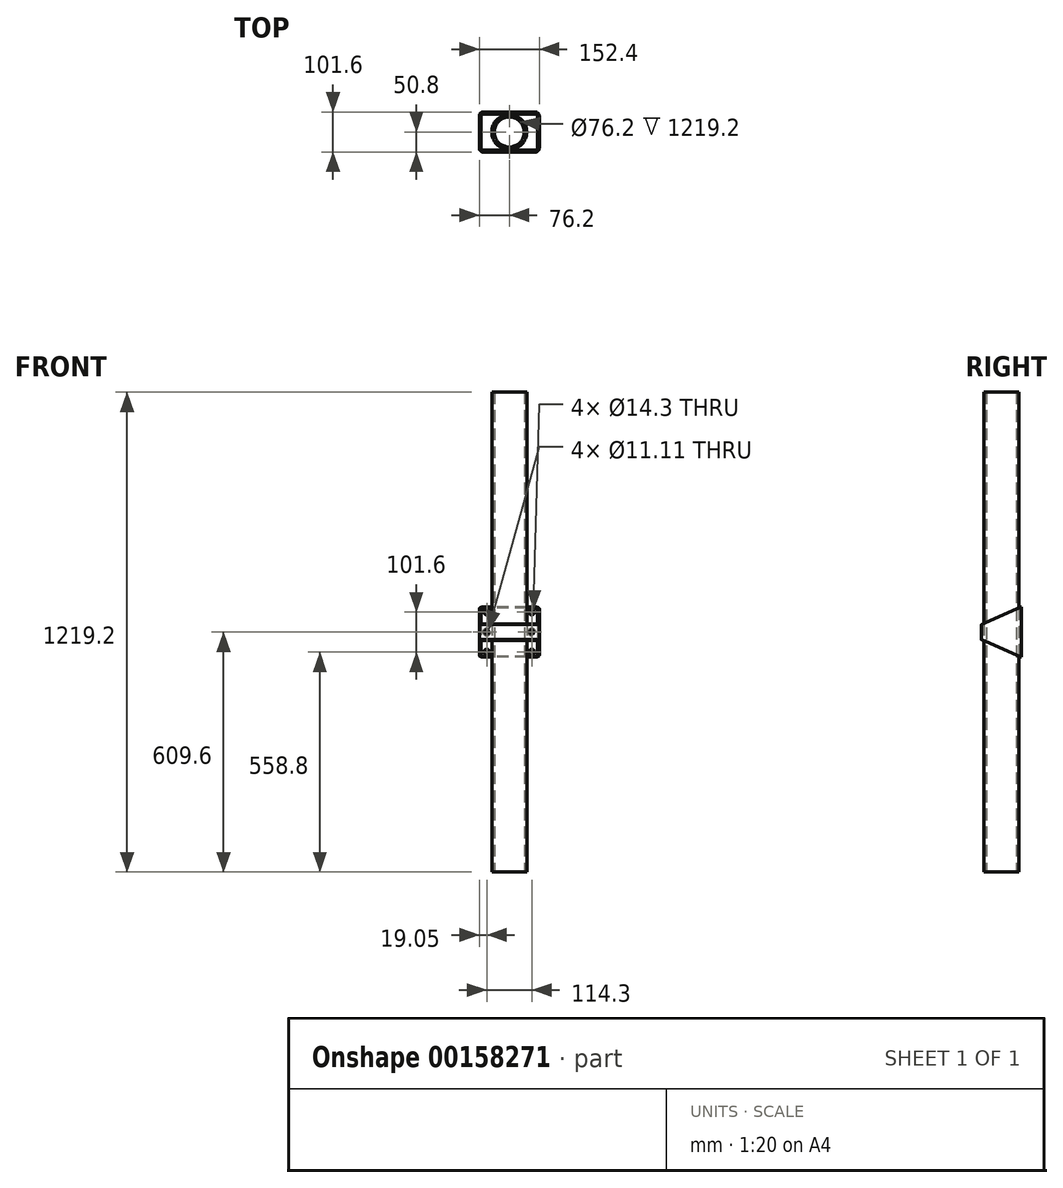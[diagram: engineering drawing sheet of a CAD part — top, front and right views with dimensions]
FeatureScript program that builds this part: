
annotation { "Feature Type Name" : "Feature", "Feature Type Description" : "" }
export const myFeature = defineFeature(function(context is Context, id is Id, definition is map)
    precondition{}
    {
        {
            var Q0;
            Q0=qCreatedBy(makeId("Top.planeOp"),FACE);
            var sketch = newSketch(context, id + "F0", { "sketchPlane" : qUnion([Q0])});
            skLineSegment(sketch, "E0.bottom", {"start": v(66.68, 50.8) * mm, "end": v(-66.67, 50.8) * mm});
            skLineSegment(sketch, "E0.top", {"start": v(66.67, -50.8) * mm, "end": v(-66.68, -50.8) * mm});
            skLineSegment(sketch, "E0.left", {"start": v(76.2, 41.28) * mm, "end": v(76.2, -41.28) * mm});
            skLineSegment(sketch, "E0.right", {"start": v(-76.2, 41.28) * mm, "end": v(-76.2, -41.27) * mm});
            skPoint(sketch, "E0.middle", {"position": v(0, 0) * mm});
            skPoint(sketch, "E1.visualSharp", {"position": v(-76.2, 50.8) * mm});
            skArc(sketch, "E1.filletArc", {"start": v(-66.67, 50.8) * mm, "mid": v(-73.41, 48.01) * mm, "end": v(-76.2, 41.28) * mm});
            skPoint(sketch, "E2.visualSharp", {"position": v(76.2, 50.8) * mm});
            skArc(sketch, "E2.filletArc", {"start": v(76.2, 41.28) * mm, "mid": v(73.41, 48.01) * mm, "end": v(66.68, 50.8) * mm});
            skPoint(sketch, "E3.visualSharp", {"position": v(76.2, -50.8) * mm});
            skArc(sketch, "E3.filletArc", {"start": v(66.67, -50.8) * mm, "mid": v(73.41, -48.01) * mm, "end": v(76.2, -41.28) * mm});
            skPoint(sketch, "E4.visualSharp", {"position": v(-76.2, -50.8) * mm});
            skArc(sketch, "E4.filletArc", {"start": v(-76.2, -41.27) * mm, "mid": v(-73.41, -48.01) * mm, "end": v(-66.68, -50.8) * mm});
            skArc(sketch, "E5.0", {"start": v(71.44, 41.27) * mm, "mid": v(70.04, 44.64) * mm, "end": v(66.68, 46.04) * mm});
            skLineSegment(sketch, "E5.1", {"start": v(66.68, 46.04) * mm, "end": v(-66.67, 46.04) * mm});
            skLineSegment(sketch, "E5.2", {"start": v(71.44, 41.27) * mm, "end": v(71.44, -41.28) * mm});
            skArc(sketch, "E5.3", {"start": v(-66.67, 46.04) * mm, "mid": v(-70.04, 44.64) * mm, "end": v(-71.44, 41.27) * mm});
            skArc(sketch, "E5.4", {"start": v(66.67, -46.04) * mm, "mid": v(70.04, -44.64) * mm, "end": v(71.44, -41.28) * mm});
            skLineSegment(sketch, "E5.5", {"start": v(66.67, -46.04) * mm, "end": v(-66.68, -46.04) * mm});
            skArc(sketch, "E5.6", {"start": v(-71.44, -41.28) * mm, "mid": v(-70.04, -44.64) * mm, "end": v(-66.68, -46.04) * mm});
            skLineSegment(sketch, "E5.7", {"start": v(-71.44, 41.27) * mm, "end": v(-71.44, -41.28) * mm});
            skSolve(sketch);
        }
        {
            var Q0;
            Q0=qCreatedBy(makeId("Right.planeOp"),FACE);
            var sketch = newSketch(context, id + "F1", { "sketchPlane" : qUnion([Q0])});
            skLineSegment(sketch, "E6", {"start": v(-50.52, 0) * mm, "end": v(-50.52, 19.05) * mm});
            skLineSegment(sketch, "E7", {"start": v(50.64, 0) * mm, "end": v(50.64, 63.5) * mm});
            skSolve(sketch);
        }
        {
            var Q0;
            Q0=qCreatedBy(makeId("Right.planeOp"),FACE);
            cPlane(context, id + "F2", {"entities" : qUnion([Q0]), "cplaneType" : CPlaneType.OFFSET, "offset" : 25.4 * mm, "width" : 152.4 * mm, "height" : 152.4 * mm});
        }
        {
            var Q0;
            Q0=qCreatedBy(id+"F2.planeOp",FACE);
            var sketch = newSketch(context, id + "F3", { "sketchPlane" : qUnion([Q0])});
            skLineSegment(sketch, "E8.0", {"start": v(50.64, 0) * mm, "end": v(50.64, 63.5) * mm});
            skSolve(sketch);
        }
        {
            var Q0;
            Q0=sQuery(id+"F1.wireOp",VERTEX,"E7.end");
            var Q1;
            Q1=sQuery(id+"F3.wireOp",VERTEX,"E8.0.end");
            var Q2;
            Q2=sQuery(id+"F1.wireOp",VERTEX,"E6.end");
            cPlane(context, id + "F4", {"entities" : qUnion([Q0, Q1, Q2]), "cplaneType" : CPlaneType.THREE_POINT, "offset" : 25.4 * mm, "width" : 152.4 * mm, "height" : 152.4 * mm});
        }
        {
            var Q0;
            Q0=makeQuery(id+"F0.imprint","IMPRINT",FACE,{"disambiguationData":[TD([[makeQuery(id+"F0.imprint","IMPRINT",EDGE,{"derivedFrom":sQuery(id+"F0.wireOp",EDGE,"E0.bottom")}),1.0]])]});
            var Q1;
            Q1=qCreatedBy(id+"F4.planeOp",FACE);
            extrude(context, id + "F5", {"entities" : qUnion([Q0]), "endBound" : BoundingType.UP_TO_SURFACE, "endBoundEntityFace" : qUnion([Q1]), "depth" : 25.4 * mm});
        }
        {
            var Q0;
            Q0=makeQuery(id+"F5.opExtrude","SWEPT_BODY",BODY,{"disambiguationData":[OSD([sQuery(id+"F0.wireOp",EDGE,"E0.bottom"),sQuery(id+"F0.wireOp",EDGE,"E0.top"),sQuery(id+"F0.wireOp",EDGE,"E0.left"),sQuery(id+"F0.wireOp",EDGE,"E0.right"),sQuery(id+"F0.wireOp",EDGE,"E1.filletArc"),sQuery(id+"F0.wireOp",EDGE,"E2.filletArc"),sQuery(id+"F0.wireOp",EDGE,"E3.filletArc"),sQuery(id+"F0.wireOp",EDGE,"E4.filletArc"),sQuery(id+"F0.wireOp",EDGE,"E5.0"),sQuery(id+"F0.wireOp",EDGE,"E5.1"),sQuery(id+"F0.wireOp",EDGE,"E5.2"),sQuery(id+"F0.wireOp",EDGE,"E5.3"),sQuery(id+"F0.wireOp",EDGE,"E5.4"),sQuery(id+"F0.wireOp",EDGE,"E5.5"),sQuery(id+"F0.wireOp",EDGE,"E5.6"),sQuery(id+"F0.wireOp",EDGE,"E5.7")])]});
            var Q1;
            Q1=qCreatedBy(makeId("Top.planeOp"),FACE);
            mirror(context, id + "F6", {"operationType" : NewBodyOperationType.ADD, "entities" : qUnion([Q0]), "mirrorPlane" : qUnion([Q1])});
        }
        {
            var Q0;
            Q0=qCreatedBy(makeId("Top.planeOp"),FACE);
            var sketch = newSketch(context, id + "F7", { "sketchPlane" : qUnion([Q0])});
            skCircle(sketch, "E9", {"center": v(0, 0) * mm, "radius": 44.45 * mm});
            skCircle(sketch, "E10.0", {"center": v(0, 0) * mm, "radius": 38.1 * mm});
            skSolve(sketch);
        }
        {
            var Q0;
            Q0 = qSketchRegion(id + "F7", true);
            extrude(context, id + "F8", {"entities" : qUnion([Q0]), "depth" : 609.6 * mm, "hasSecondDirection" : true, "secondDirectionOppositeDirection" : true, "secondDirectionDepth" : 609.6 * mm});
        }
        {
            var Q0;
            {var subQ0=makeQuery(id+"F5.opExtrude","SWEPT_FACE",FACE,{"disambiguationData":[OSD([sQuery(id+"F0.wireOp",EDGE,"E0.bottom")])]});Q0=makeQuery(id+"F6.boolean.opBoolean","MERGE",FACE,{"derivedFrom":[subQ0,makeQuery(id+"F6.opPattern","COPY",FACE,{"derivedFrom":subQ0,"instanceName":"1"})]});}
            var sketch = newSketch(context, id + "F9", { "sketchPlane" : qUnion([Q0])});
            skPoint(sketch, "E11", {"position": v(57.15, 0) * mm});
            skPoint(sketch, "E12", {"position": v(57.15, 50.8) * mm});
            skPoint(sketch, "E13.MirrorP", {"position": v(57.15, -50.8) * mm});
            skPoint(sketch, "E14.MirrorP", {"position": v(-57.15, 50.8) * mm});
            skPoint(sketch, "E15.MirrorP", {"position": v(-57.15, 0) * mm});
            skPoint(sketch, "E16.MirrorP", {"position": v(-57.15, -50.8) * mm});
            skSolve(sketch);
        }
        {
            var Q0;
            Q0=sQuery(id+"F9.wireOp",VERTEX,"E14.MirrorP");
            var Q1;
            Q1=sQuery(id+"F9.wireOp",VERTEX,"E12");
            var Q2;
            Q2=sQuery(id+"F9.wireOp",VERTEX,"E13.MirrorP");
            var Q3;
            Q3=sQuery(id+"F9.wireOp",VERTEX,"E16.MirrorP");
            var Q4;
            Q4=makeQuery(id+"F5.opExtrude","SWEPT_BODY",BODY,{"disambiguationData":[OSD([sQuery(id+"F0.wireOp",EDGE,"E0.bottom"),sQuery(id+"F0.wireOp",EDGE,"E0.top"),sQuery(id+"F0.wireOp",EDGE,"E0.left"),sQuery(id+"F0.wireOp",EDGE,"E0.right"),sQuery(id+"F0.wireOp",EDGE,"E1.filletArc"),sQuery(id+"F0.wireOp",EDGE,"E2.filletArc"),sQuery(id+"F0.wireOp",EDGE,"E3.filletArc"),sQuery(id+"F0.wireOp",EDGE,"E4.filletArc"),sQuery(id+"F0.wireOp",EDGE,"E5.0"),sQuery(id+"F0.wireOp",EDGE,"E5.1"),sQuery(id+"F0.wireOp",EDGE,"E5.2"),sQuery(id+"F0.wireOp",EDGE,"E5.3"),sQuery(id+"F0.wireOp",EDGE,"E5.4"),sQuery(id+"F0.wireOp",EDGE,"E5.5"),sQuery(id+"F0.wireOp",EDGE,"E5.6"),sQuery(id+"F0.wireOp",EDGE,"E5.7")])]});
            hole(context, id + "F10", {"style" : HoleStyle.SIMPLE, "endStyle" : HoleEndStyle.THROUGH, "holeDiameter" : 14.3 * mm, "locations" : qUnion([Q0, Q1, Q2, Q3]), "scope" : qUnion([Q4]), "isTappedThrough" : true});
        }
        {
            var Q0;
            Q0=sQuery(id+"F9.wireOp",VERTEX,"E15.MirrorP");
            var Q1;
            Q1=sQuery(id+"F9.wireOp",VERTEX,"E11");
            var Q2;
            Q2=makeQuery(id+"F5.opExtrude","SWEPT_BODY",BODY,{"disambiguationData":[OSD([sQuery(id+"F0.wireOp",EDGE,"E0.bottom"),sQuery(id+"F0.wireOp",EDGE,"E0.top"),sQuery(id+"F0.wireOp",EDGE,"E0.left"),sQuery(id+"F0.wireOp",EDGE,"E0.right"),sQuery(id+"F0.wireOp",EDGE,"E1.filletArc"),sQuery(id+"F0.wireOp",EDGE,"E2.filletArc"),sQuery(id+"F0.wireOp",EDGE,"E3.filletArc"),sQuery(id+"F0.wireOp",EDGE,"E4.filletArc"),sQuery(id+"F0.wireOp",EDGE,"E5.0"),sQuery(id+"F0.wireOp",EDGE,"E5.1"),sQuery(id+"F0.wireOp",EDGE,"E5.2"),sQuery(id+"F0.wireOp",EDGE,"E5.3"),sQuery(id+"F0.wireOp",EDGE,"E5.4"),sQuery(id+"F0.wireOp",EDGE,"E5.5"),sQuery(id+"F0.wireOp",EDGE,"E5.6"),sQuery(id+"F0.wireOp",EDGE,"E5.7")])]});
            hole(context, id + "F11", {"style" : HoleStyle.C_SINK, "endStyle" : HoleEndStyle.THROUGH, "holeDiameter" : 11.1 * mm, "cSinkDiameter" : 19.05 * mm, "cSinkAngle" : 90 * degree, "locations" : qUnion([Q0, Q1]), "scope" : qUnion([Q2]), "isTappedThrough" : true});
        }
    });
